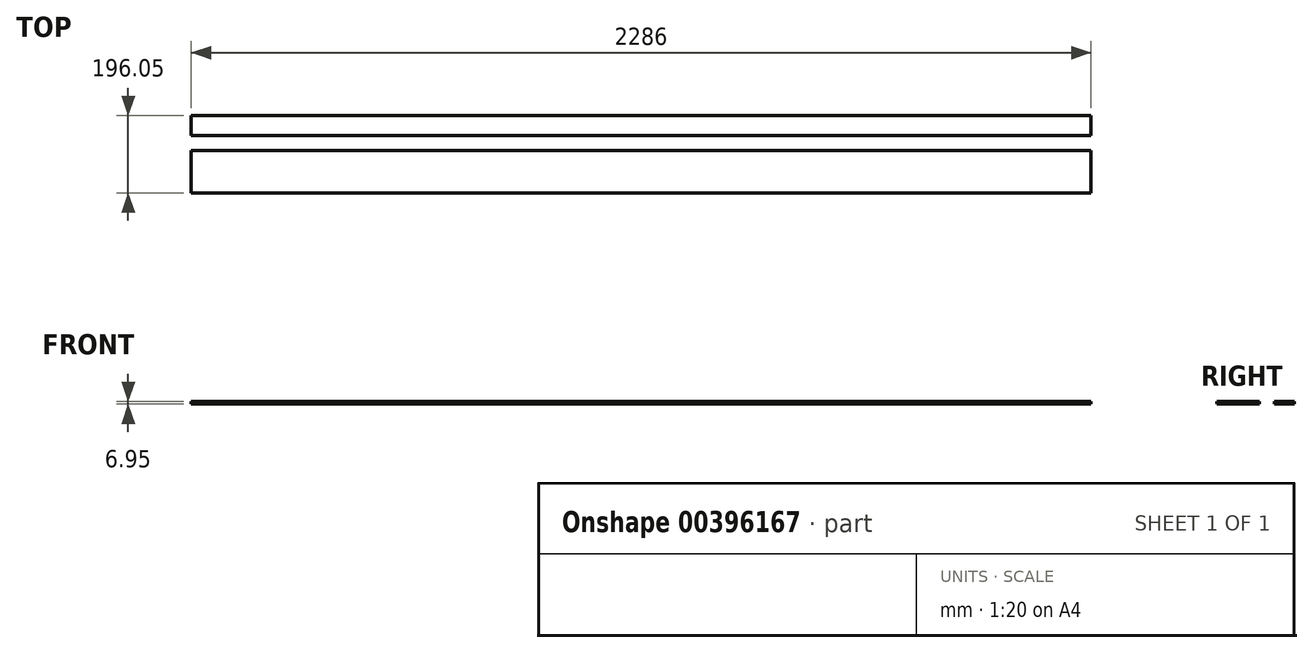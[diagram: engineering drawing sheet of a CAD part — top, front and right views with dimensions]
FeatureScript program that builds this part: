
annotation { "Feature Type Name" : "Feature", "Feature Type Description" : "" }
export const myFeature = defineFeature(function(context is Context, id is Id, definition is map)
    precondition{}
    {
        {
            var Q0;
            Q0=qCreatedBy(makeId("Right.planeOp"),FACE);
            var sketch = newSketch(context, id + "F0", { "sketchPlane" : qUnion([Q0])});
            skLineSegment(sketch, "E0.bottom", {"start": v(-20.92, -1.48) * mm, "end": v(-128.66, -1.48) * mm});
            skLineSegment(sketch, "E0.top", {"start": v(-20.92, 4.87) * mm, "end": v(-128.66, 4.87) * mm});
            skLineSegment(sketch, "E0.left", {"start": v(-20.92, -1.48) * mm, "end": v(-20.92, 4.87) * mm});
            skLineSegment(sketch, "E0.right", {"start": v(-128.66, -1.48) * mm, "end": v(-128.66, 4.87) * mm});
            skPoint(sketch, "E0.middle", {"position": v(-74.8, 1.7) * mm});
            skLineSegment(sketch, "E1.bottom", {"start": v(67.4, -0.88) * mm, "end": v(16.6, -0.88) * mm});
            skLineSegment(sketch, "E1.top", {"start": v(67.4, 5.47) * mm, "end": v(16.6, 5.47) * mm});
            skLineSegment(sketch, "E1.left", {"start": v(67.4, -0.88) * mm, "end": v(67.4, 5.47) * mm});
            skLineSegment(sketch, "E1.right", {"start": v(16.6, -0.88) * mm, "end": v(16.6, 5.47) * mm});
            skPoint(sketch, "E1.middle", {"position": v(42, 2.3) * mm});
            skSolve(sketch);
        }
        {
            var Q0;
            Q0=makeQuery(id+"F0.imprint","IMPRINT",FACE,{"disambiguationData":[TD([[makeQuery(id+"F0.imprint","IMPRINT",EDGE,{"derivedFrom":sQuery(id+"F0.wireOp",EDGE,"E0.bottom")}),-1.0]])]});
            extrude(context, id + "F1", {"entities" : qUnion([Q0]), "depth" : 2286 * mm});
        }
        {
            var Q0;
            Q0=makeQuery(id+"F0.imprint","IMPRINT",FACE,{"disambiguationData":[TD([[makeQuery(id+"F0.imprint","IMPRINT",EDGE,{"derivedFrom":sQuery(id+"F0.wireOp",EDGE,"E1.bottom")}),-1.0]])]});
            extrude(context, id + "F2", {"entities" : qUnion([Q0]), "depth" : 2286 * mm});
        }
    });
